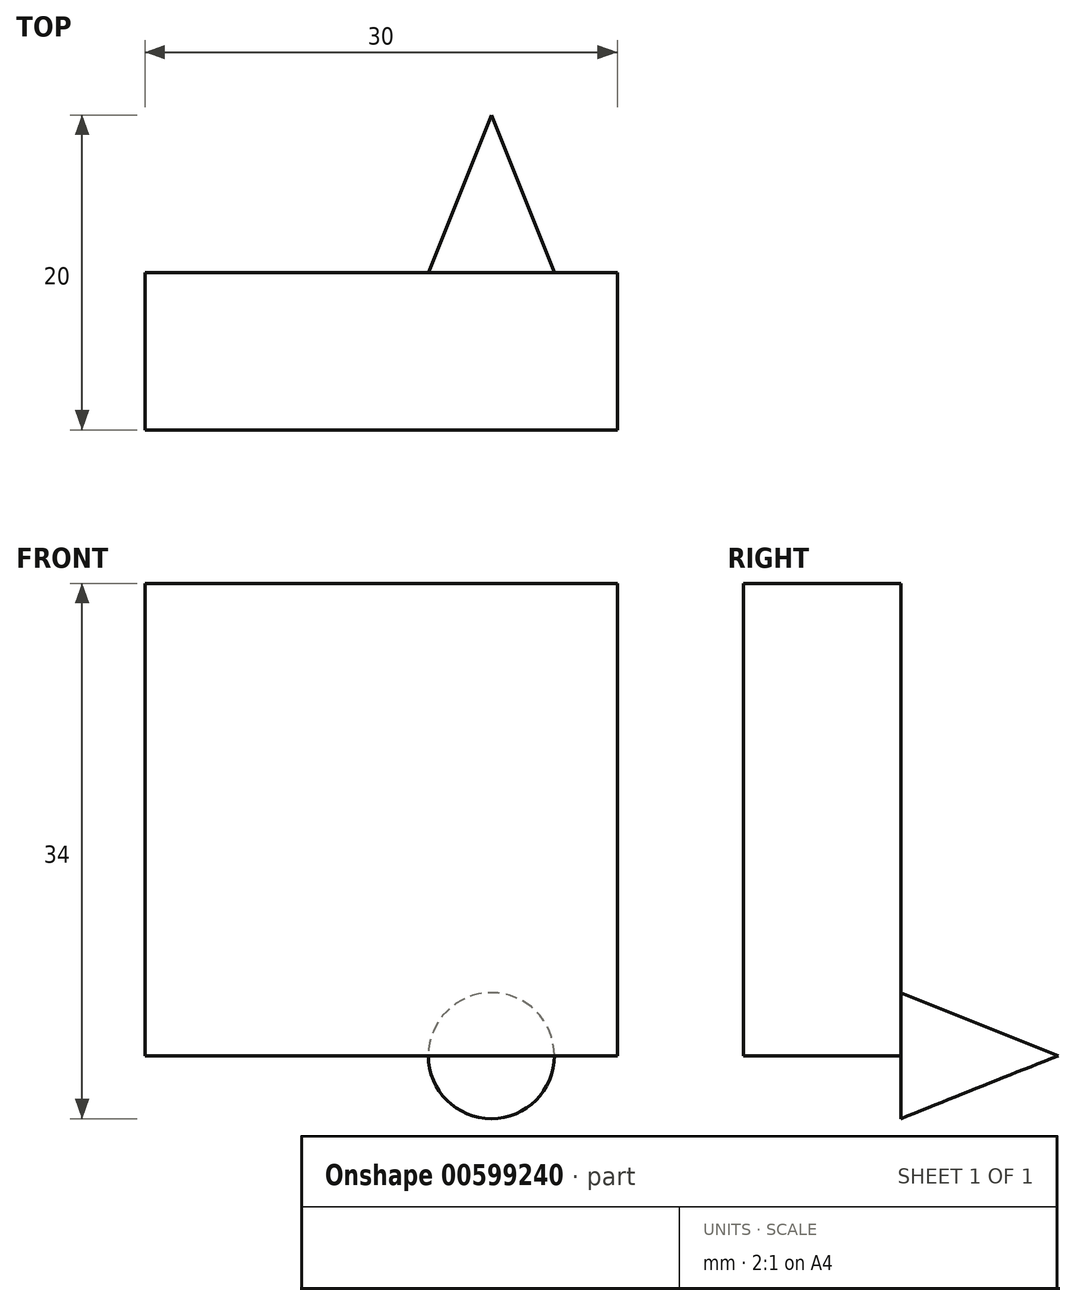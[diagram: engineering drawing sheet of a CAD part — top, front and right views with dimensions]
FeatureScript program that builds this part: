
annotation { "Feature Type Name" : "Feature", "Feature Type Description" : "" }
export const myFeature = defineFeature(function(context is Context, id is Id, definition is map)
    precondition{}
    {
        {
            var Q0;
            Q0=qCreatedBy(makeId("Front.planeOp"),FACE);
            var sketch = newSketch(context, id + "F0", { "sketchPlane" : qUnion([Q0])});
            skLineSegment(sketch, "E0.bottom", {"start": v(0, 30) * mm, "end": v(30, 30) * mm});
            skLineSegment(sketch, "E0.top", {"start": v(0, 0) * mm, "end": v(30, 0) * mm});
            skLineSegment(sketch, "E0.left", {"start": v(0, 30) * mm, "end": v(0, 0) * mm});
            skLineSegment(sketch, "E0.right", {"start": v(30, 30) * mm, "end": v(30, 0) * mm});
            skSolve(sketch);
        }
        {
            var Q0;
            Q0=makeQuery(id+"F0.imprint","IMPRINT",FACE,{"disambiguationData":[TD([[makeQuery(id+"F0.imprint","IMPRINT",EDGE,{"derivedFrom":sQuery(id+"F0.wireOp",EDGE,"E0.bottom")}),-1.0]])]});
            extrude(context, id + "F1", {"entities" : qUnion([Q0]), "oppositeDirection" : true, "depth" : 10 * mm, "offsetDistance" : 25 * mm});
        }
        {
            var Q0;
            Q0=makeQuery(id+"F1.opExtrude","CAP_FACE",FACE,{"disambiguationData":[OSD([sQuery(id+"F0.wireOp",EDGE,"E0.bottom"),sQuery(id+"F0.wireOp",EDGE,"E0.top"),sQuery(id+"F0.wireOp",EDGE,"E0.left"),sQuery(id+"F0.wireOp",EDGE,"E0.right")])],"isStart":false});
            var sketch = newSketch(context, id + "F2", { "sketchPlane" : qUnion([Q0])});
            skCircle(sketch, "E1", {"center": v(-22, 8) * mm, "radius": 4.42 * mm});
            skSolve(sketch);
        }
        {
            var Q0;
            Q0=qCreatedBy(makeId("Top.planeOp"),FACE);
            var sketch = newSketch(context, id + "F3", { "sketchPlane" : qUnion([Q0])});
            skLineSegment(sketch, "E2", {"start": v(22, 10) * mm, "end": v(22, 20) * mm});
            skLineSegment(sketch, "E3", {"start": v(22, 20) * mm, "end": v(26, 10) * mm});
            skLineSegment(sketch, "E4", {"start": v(26, 10) * mm, "end": v(22, 10) * mm});
            skPoint(sketch, "E5.endSnap0", {"position": v(24, 10) * mm});
            skLineSegment(sketch, "E6.0.0", {"start": v(0, 0) * mm, "end": v(30, 0) * mm, "construction": true});
            skLineSegment(sketch, "E6.0.1", {"start": v(30, 0) * mm, "end": v(30, 10) * mm, "construction": true});
            skLineSegment(sketch, "E6.0.2", {"start": v(30, 10) * mm, "end": v(0, 10) * mm, "construction": true});
            skLineSegment(sketch, "E6.0.3", {"start": v(0, 10) * mm, "end": v(0, 0) * mm, "construction": true});
            skSolve(sketch);
        }
        {
            var Q0;
            Q0 = qSketchRegion(id + "F3", true);
            var Q1;
            Q1=sQuery(id+"F3.wireOp",EDGE,"E2");
            revolve(context, id + "F4", {"operationType" : NewBodyOperationType.ADD, "entities" : qUnion([Q0]), "axis" : qUnion([Q1]), "revolveType" : RevolveType.FULL});
        }
    });
